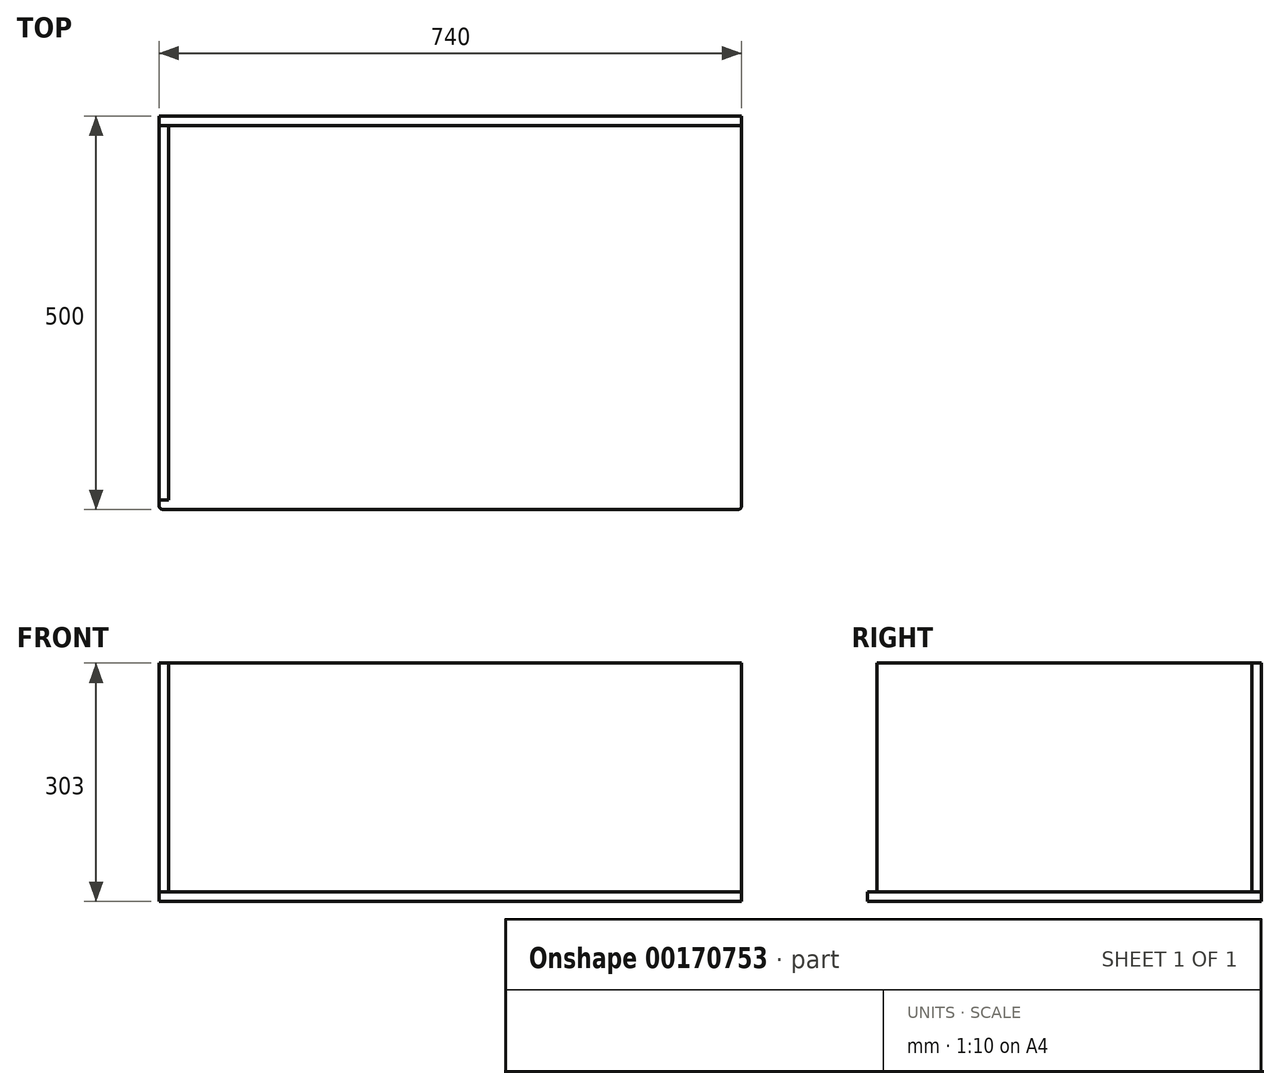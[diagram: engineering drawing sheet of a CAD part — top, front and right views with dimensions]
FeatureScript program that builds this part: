
annotation { "Feature Type Name" : "Feature", "Feature Type Description" : "" }
export const myFeature = defineFeature(function(context is Context, id is Id, definition is map)
    precondition{}
    {
        {
            var Q0;
            Q0=qCreatedBy(makeId("Top.planeOp"),FACE);
            var sketch = newSketch(context, id + "F0", { "sketchPlane" : qUnion([Q0])});
            skLineSegment(sketch, "E0.bottom", {"start": v(370, -250) * mm, "end": v(-370, -250) * mm});
            skLineSegment(sketch, "E0.top", {"start": v(370, 250) * mm, "end": v(-370, 250) * mm});
            skLineSegment(sketch, "E0.left", {"start": v(370, -250) * mm, "end": v(370, 250) * mm});
            skLineSegment(sketch, "E0.right", {"start": v(-370, -250) * mm, "end": v(-370, 250) * mm});
            skPoint(sketch, "E0.middle", {"position": v(0, 0) * mm});
            skLineSegment(sketch, "E1", {"start": v(-370, 238) * mm, "end": v(370, 238) * mm});
            skLineSegment(sketch, "E2", {"start": v(-358, 238) * mm, "end": v(-358, -250) * mm});
            skLineSegment(sketch, "E3.MirrorCS", {"start": v(358, 238) * mm, "end": v(358, -250) * mm});
            skLineSegment(sketch, "E4", {"start": v(-370, -238) * mm, "end": v(-358, -238) * mm});
            skSolve(sketch);
        }
        {
            var Q0;
            Q0 = qSketchRegion(id + "F0", true);
            extrude(context, id + "F1", {"entities" : qUnion([Q0]), "oppositeDirection" : true, "depth" : 12 * mm});
        }
        {
            var Q0;
            {var subQ4=sQuery(id+"F0.wireOp",EDGE,"E0.top");Q0=makeQuery(id+"F0.imprint","IMPRINT",FACE,{"disambiguationData":[TD([[makeQuery(id+"F0.imprint","IMPRINT",EDGE,{"derivedFrom":subQ4}),1.0]])]});}
            extrude(context, id + "F2", {"entities" : qUnion([Q0]), "depth" : 291 * mm});
        }
        {
            var Q0;
            {var subQ3=sQuery(id+"F0.wireOp",EDGE,"E4");Q0=makeQuery(id+"F0.imprint","IMPRINT",FACE,{"disambiguationData":[TD([[makeQuery(id+"F0.imprint","IMPRINT",EDGE,{"derivedFrom":subQ3}),1.0]])]});}
            extrude(context, id + "F3", {"entities" : qUnion([Q0]), "depth" : 291 * mm});
        }
        {
            var Q0;
            Q0=makeQuery(id+"F1.opExtrude","SWEPT_EDGE",EDGE,{"disambiguationData":[OSD([sQuery(id+"F0.wireOp",EDGE,"E0.bottom"),sQuery(id+"F0.wireOp",EDGE,"E0.left")])]});
            var Q1;
            Q1=makeQuery(id+"F1.opExtrude","SWEPT_EDGE",EDGE,{"disambiguationData":[OSD([sQuery(id+"F0.wireOp",EDGE,"E0.bottom"),sQuery(id+"F0.wireOp",EDGE,"E0.right")])]});
            fillet(context, id + "F4", {"entities" : qUnion([Q0, Q1]), "radius" : 5 * mm, "tangentPropagation" : true, "allowEdgeOverflow" : false});
        }
    });
